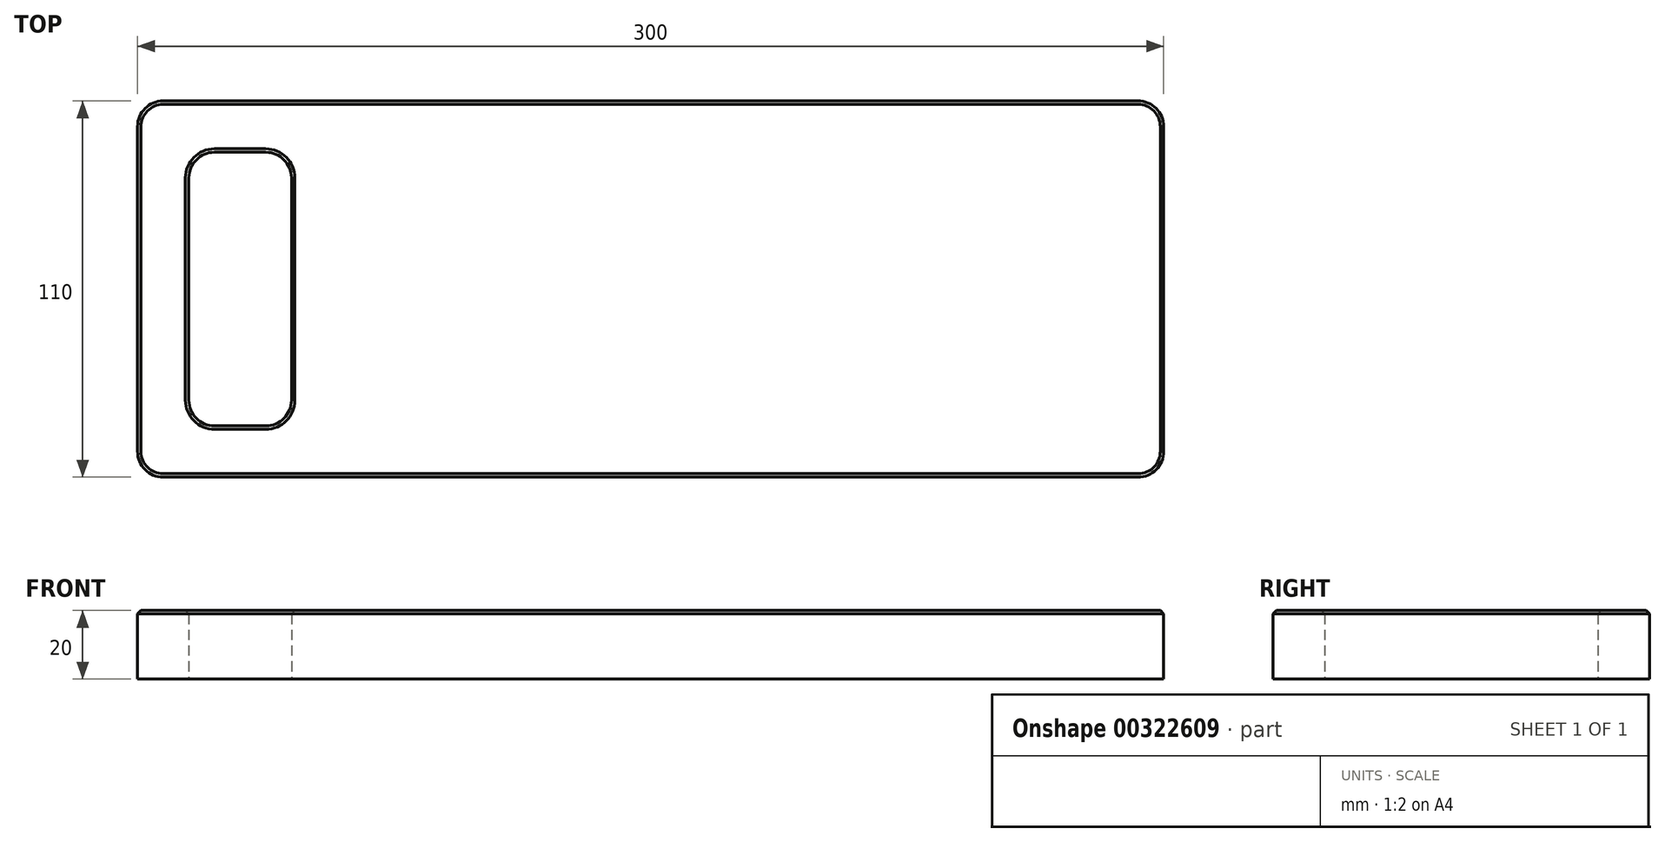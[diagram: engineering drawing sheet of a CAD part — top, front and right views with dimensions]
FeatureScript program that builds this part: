
annotation { "Feature Type Name" : "Feature", "Feature Type Description" : "" }
export const myFeature = defineFeature(function(context is Context, id is Id, definition is map)
    precondition{}
    {
        {
            var Q0;
            Q0=qCreatedBy(makeId("Top.planeOp"),FACE);
            var sketch = newSketch(context, id + "F0", { "sketchPlane" : qUnion([Q0])});
            skLineSegment(sketch, "E0", {"start": v(0, 0) * mm, "end": v(300, 0) * mm});
            skLineSegment(sketch, "E1", {"start": v(300, 0) * mm, "end": v(300, 110) * mm});
            skLineSegment(sketch, "E2", {"start": v(300, 110) * mm, "end": v(0, 110) * mm});
            skLineSegment(sketch, "E3", {"start": v(0, 110) * mm, "end": v(0, 0) * mm});
            skLineSegment(sketch, "E4", {"start": v(15, 55) * mm, "end": v(15, 87.5) * mm});
            skLineSegment(sketch, "E5", {"start": v(15, 55) * mm, "end": v(15, 22.5) * mm});
            skLineSegment(sketch, "E6", {"start": v(22.5, 95) * mm, "end": v(37.5, 95) * mm});
            skLineSegment(sketch, "E7", {"start": v(45, 87.5) * mm, "end": v(45, 22.5) * mm});
            skLineSegment(sketch, "E8", {"start": v(22.5, 15) * mm, "end": v(37.5, 15) * mm});
            skLineSegment(sketch, "E9", {"start": v(15, 55) * mm, "end": v(0, 55) * mm});
            skPoint(sketch, "E10.visualSharp", {"position": v(15, 95) * mm});
            skArc(sketch, "E10.filletArc", {"start": v(22.5, 95) * mm, "mid": v(17.2, 92.8) * mm, "end": v(15, 87.5) * mm});
            skPoint(sketch, "E11.visualSharp", {"position": v(45, 95) * mm});
            skArc(sketch, "E11.filletArc", {"start": v(45, 87.5) * mm, "mid": v(42.8, 92.8) * mm, "end": v(37.5, 95) * mm});
            skPoint(sketch, "E12.visualSharp", {"position": v(15, 15) * mm});
            skArc(sketch, "E12.filletArc", {"start": v(15, 22.5) * mm, "mid": v(17.2, 17.2) * mm, "end": v(22.5, 15) * mm});
            skPoint(sketch, "E13.visualSharp", {"position": v(45, 15) * mm});
            skArc(sketch, "E13.filletArc", {"start": v(37.5, 15) * mm, "mid": v(42.8, 17.2) * mm, "end": v(45, 22.5) * mm});
            skSolve(sketch);
        }
        {
            var Q0;
            Q0=makeQuery(id+"F0.imprint","IMPRINT",FACE,{"disambiguationData":[TD([[makeQuery(id+"F0.imprint","IMPRINT",EDGE,{"derivedFrom":sQuery(id+"F0.wireOp",EDGE,"E0")}),1.0]])]});
            extrude(context, id + "F1", {"entities" : qUnion([Q0]), "depth" : 20 * mm, "offsetDistance" : 25 * mm});
        }
        {
            var Q0;
            Q0=makeQuery(id+"F1.opExtrude","SWEPT_EDGE",EDGE,{"disambiguationData":[OSD([sQuery(id+"F0.wireOp",EDGE,"E0"),sQuery(id+"F0.wireOp",EDGE,"E1")])]});
            var Q1;
            Q1=makeQuery(id+"F1.opExtrude","SWEPT_EDGE",EDGE,{"disambiguationData":[OSD([sQuery(id+"F0.wireOp",EDGE,"E1"),sQuery(id+"F0.wireOp",EDGE,"E2")])]});
            var Q2;
            Q2=makeQuery(id+"F1.opExtrude","SWEPT_EDGE",EDGE,{"disambiguationData":[OSD([sQuery(id+"F0.wireOp",EDGE,"E0"),sQuery(id+"F0.wireOp",EDGE,"E3")])]});
            var Q3;
            Q3=makeQuery(id+"F1.opExtrude","SWEPT_EDGE",EDGE,{"disambiguationData":[OSD([sQuery(id+"F0.wireOp",EDGE,"E2"),sQuery(id+"F0.wireOp",EDGE,"E3")])]});
            fillet(context, id + "F2", {"entities" : qUnion([Q0, Q1, Q2, Q3]), "radius" : 7.5 * mm, "tangentPropagation" : true, "allowEdgeOverflow" : false});
        }
        {
            var Q0;
            Q0=makeQuery(id+"F1.opExtrude","CAP_FACE",FACE,{"disambiguationData":[OSD([sQuery(id+"F0.wireOp",EDGE,"E0"),sQuery(id+"F0.wireOp",EDGE,"E1"),sQuery(id+"F0.wireOp",EDGE,"E2"),sQuery(id+"F0.wireOp",EDGE,"E3"),sQuery(id+"F0.wireOp",EDGE,"E4"),sQuery(id+"F0.wireOp",EDGE,"E5"),sQuery(id+"F0.wireOp",EDGE,"E6"),sQuery(id+"F0.wireOp",EDGE,"E7"),sQuery(id+"F0.wireOp",EDGE,"E8"),sQuery(id+"F0.wireOp",EDGE,"E10.filletArc"),sQuery(id+"F0.wireOp",EDGE,"E11.filletArc"),sQuery(id+"F0.wireOp",EDGE,"E12.filletArc"),sQuery(id+"F0.wireOp",EDGE,"E13.filletArc")])],"isStart":false});
            chamfer(context, id + "F3", {"entities" : qUnion([Q0]), "width" : 1 * mm, "tangentPropagation" : true});
        }
    });
